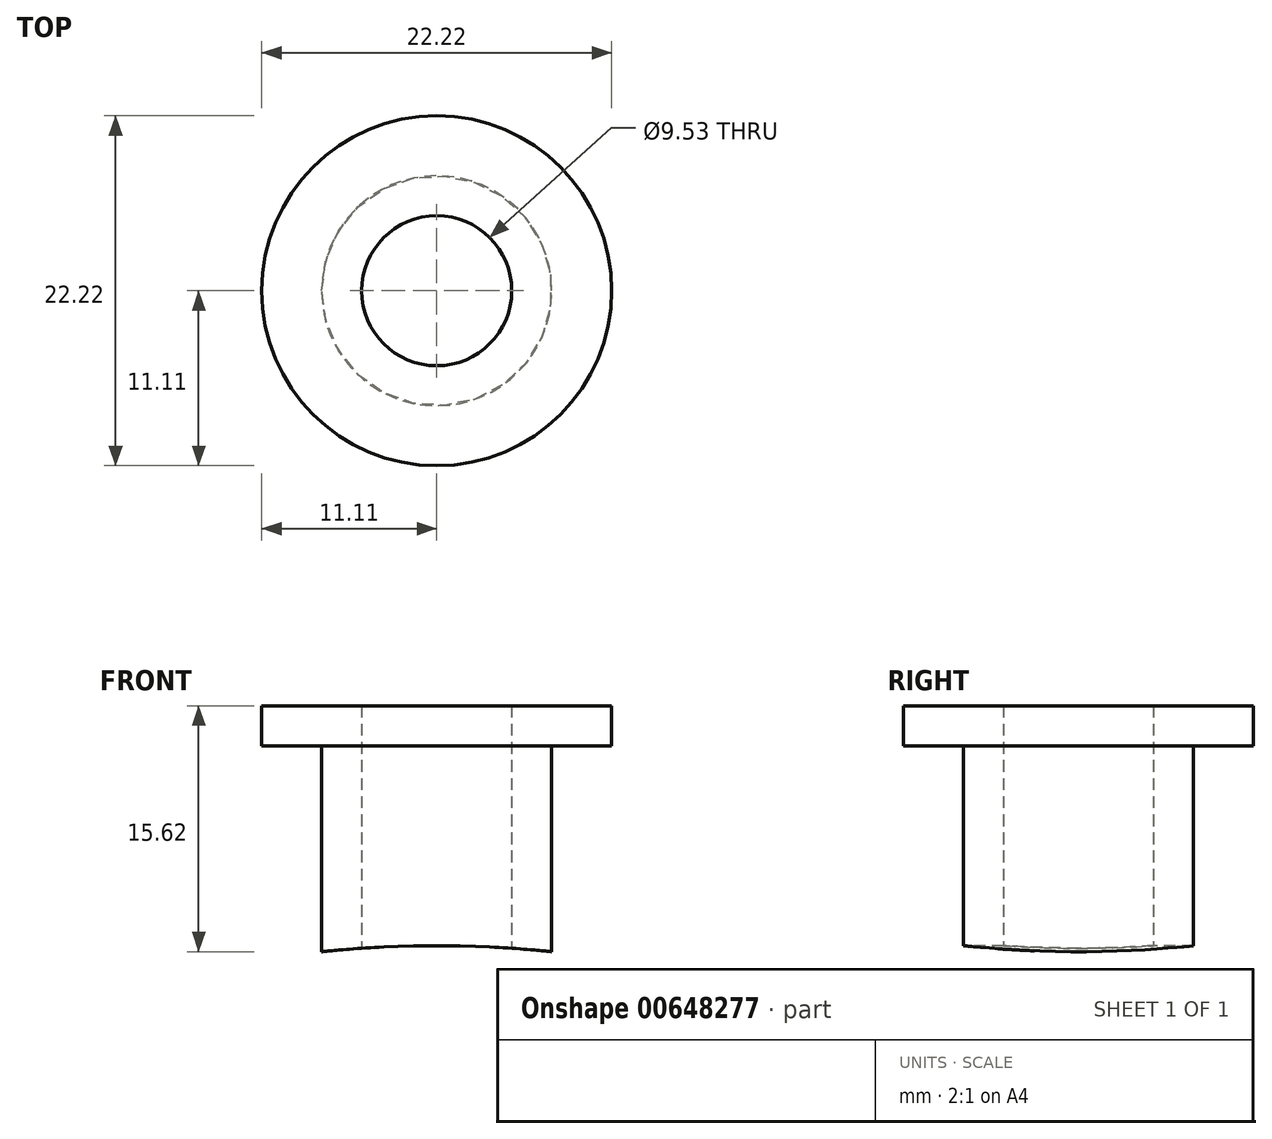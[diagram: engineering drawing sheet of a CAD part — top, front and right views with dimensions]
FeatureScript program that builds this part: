
annotation { "Feature Type Name" : "Feature", "Feature Type Description" : "" }
export const myFeature = defineFeature(function(context is Context, id is Id, definition is map)
    precondition{}
    {
        {
            var Q0;
            Q0=qCreatedBy(makeId("Front.planeOp"),FACE);
            var sketch = newSketch(context, id + "F0", { "sketchPlane" : qUnion([Q0])});
            skLineSegment(sketch, "E0", {"start": v(0, 0) * mm, "end": v(-4.76, 0) * mm, "construction": true});
            skLineSegment(sketch, "E1", {"start": v(0, 0) * mm, "end": v(0, 4.03) * mm, "construction": true});
            skLineSegment(sketch, "E2", {"start": v(-4.76, 0) * mm, "end": v(-7.3, 0) * mm});
            skLineSegment(sketch, "E3", {"start": v(-7.3, 0) * mm, "end": v(-7.3, 12.7) * mm});
            skLineSegment(sketch, "E4", {"start": v(-7.3, 12.7) * mm, "end": v(-4.76, 12.7) * mm});
            skLineSegment(sketch, "E5", {"start": v(-4.76, 12.7) * mm, "end": v(-4.76, 0) * mm});
            skLineSegment(sketch, "E6", {"start": v(-4.76, 12.7) * mm, "end": v(-4.76, 15.24) * mm});
            skLineSegment(sketch, "E7", {"start": v(-4.76, 15.24) * mm, "end": v(-11.11, 15.24) * mm});
            skLineSegment(sketch, "E8", {"start": v(-11.11, 15.24) * mm, "end": v(-11.11, 12.7) * mm});
            skLineSegment(sketch, "E9", {"start": v(-11.11, 12.7) * mm, "end": v(-7.3, 12.7) * mm});
            skSolve(sketch);
        }
        {
            var Q0;
            Q0 = qSketchRegion(id + "F0", true);
            var Q1;
            Q1=sQuery(id+"F0.wireOp",EDGE,"E1");
            revolve(context, id + "F1", {"entities" : qUnion([Q0]), "axis" : qUnion([Q1]), "revolveType" : RevolveType.FULL});
        }
        {
            var Q0;
            Q0=qCreatedBy(makeId("Front.planeOp"),FACE);
            var sketch = newSketch(context, id + "F2", { "sketchPlane" : qUnion([Q0])});
            skLineSegment(sketch, "E10", {"start": v(0, 0) * mm, "end": v(0, -69.85) * mm, "construction": true});
            skCircle(sketch, "E11", {"center": v(0, -69.85) * mm, "radius": 69.85 * mm});
            skSolve(sketch);
        }
        {
            var Q0;
            Q0=makeQuery(id+"F1.opRevolve","SWEPT_FACE",FACE,{"disambiguationData":[OSD([sQuery(id+"F0.wireOp",EDGE,"E2")])]});
            extrude(context, id + "F3", {"entities" : qUnion([Q0]), "operationType" : NewBodyOperationType.ADD, "depth" : 25.4 * mm, "offsetDistance" : 25.4 * mm});
        }
        {
            var Q0;
            Q0=makeQuery(id+"F2.imprint","IMPRINT",FACE,{"disambiguationData":[TD([[makeQuery(id+"F2.imprint","IMPRINT",EDGE,{"derivedFrom":sQuery(id+"F2.wireOp",EDGE,"E11")}),1.0]])]});
            extrude(context, id + "F4", {"entities" : qUnion([Q0]), "operationType" : NewBodyOperationType.REMOVE, "oppositeDirection" : true, "depth" : 25.4 * mm, "offsetDistance" : 25.4 * mm, "hasSecondDirection" : true, "secondDirectionOppositeDirection" : false, "secondDirectionDepth" : 25.4 * mm});
        }
    });
